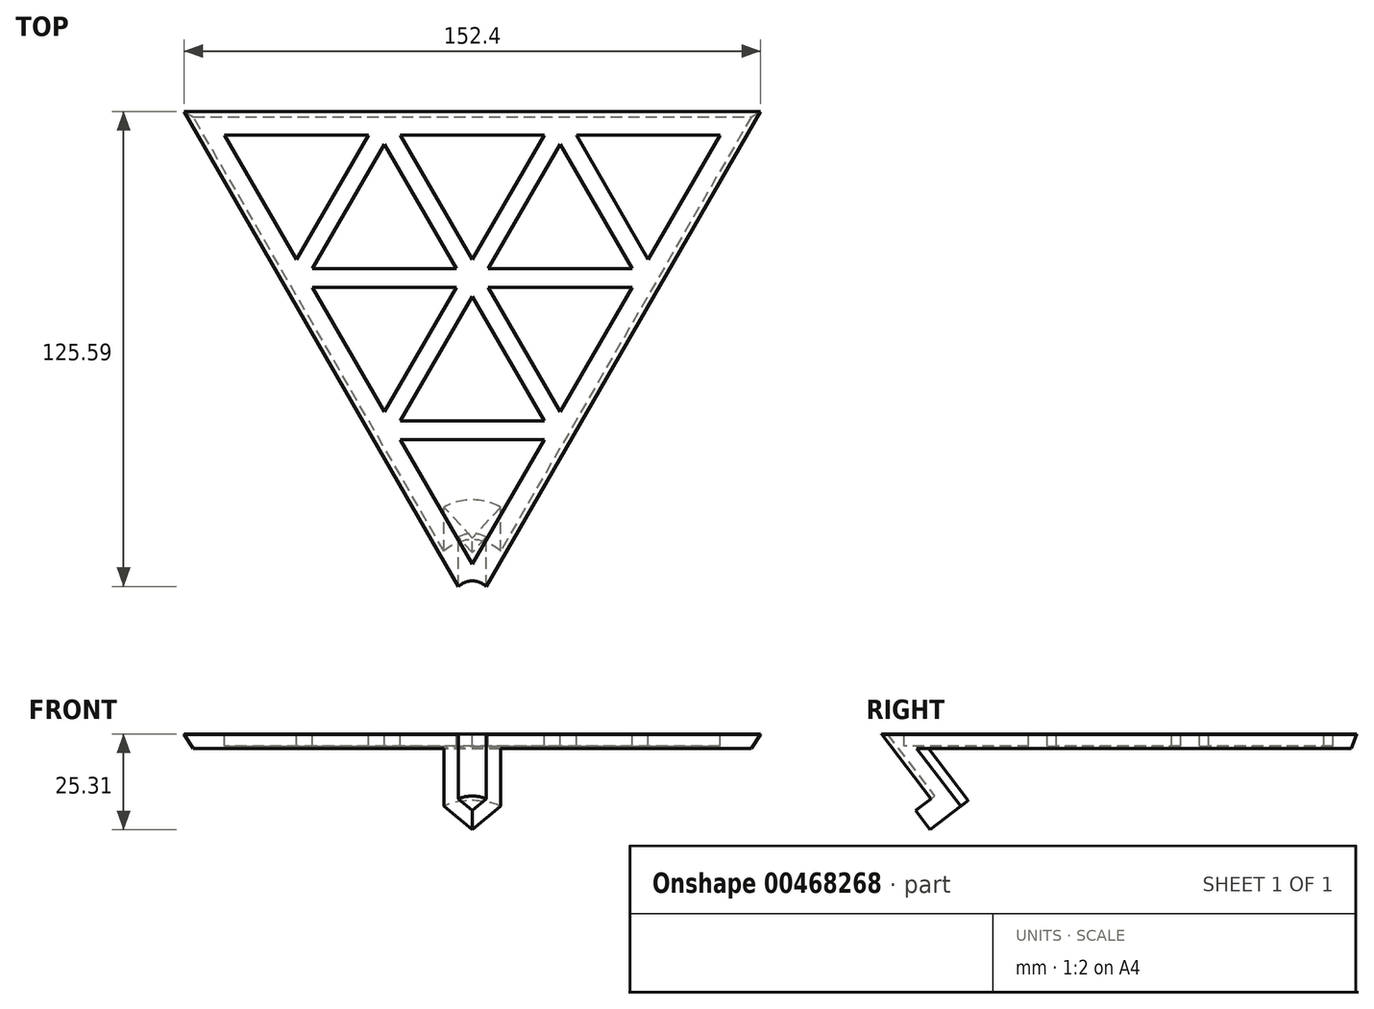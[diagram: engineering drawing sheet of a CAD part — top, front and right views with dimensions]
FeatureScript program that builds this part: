
annotation { "Feature Type Name" : "Feature", "Feature Type Description" : "" }
export const myFeature = defineFeature(function(context is Context, id is Id, definition is map)
    precondition{}
    {
        {
            var Q0;
            Q0=qCreatedBy(makeId("Top.planeOp"),FACE);
            var sketch = newSketch(context, id + "F0", { "sketchPlane" : qUnion([Q0])});
            skLineSegment(sketch, "E0", {"start": v(-76.2, 0) * mm, "end": v(76.2, 0) * mm});
            skLineSegment(sketch, "E1", {"start": v(76.2, 0) * mm, "end": v(0, -131.98) * mm});
            skLineSegment(sketch, "E2", {"start": v(0, -131.98) * mm, "end": v(-76.2, 0) * mm});
            skSolve(sketch);
        }
        {
            var Q0;
            Q0 = qSketchRegion(id + "F0", true);
            extrude(context, id + "F1", {"entities" : qUnion([Q0]), "depth" : 3.8 * mm});
        }
        {
            var Q0;
            Q0=makeQuery(id+"F1.opExtrude","CAP_EDGE",EDGE,{"disambiguationData":[OSD([sQuery(id+"F0.wireOp",EDGE,"E2")])],"isStart":true});
            var Q1;
            Q1=makeQuery(id+"F1.opExtrude","CAP_EDGE",EDGE,{"disambiguationData":[OSD([sQuery(id+"F0.wireOp",EDGE,"E1")])],"isStart":true});
            var Q2;
            Q2=makeQuery(id+"F1.opExtrude","CAP_EDGE",EDGE,{"disambiguationData":[OSD([sQuery(id+"F0.wireOp",EDGE,"E0")])],"isStart":true});
            chamfer(context, id + "F2", {"entities" : qUnion([Q0, Q1, Q2]), "chamferType" : ChamferType.OFFSET_ANGLE, "width" : 1.4 * mm, "oppositeDirection" : false, "angle" : 69.1 * degree, "tangentPropagation" : true});
        }
        {
            var Q0;
            Q0=makeQuery(id+"F1.opExtrude","CAP_FACE",FACE,{"disambiguationData":[OSD([sQuery(id+"F0.wireOp",EDGE,"E0"),sQuery(id+"F0.wireOp",EDGE,"E1"),sQuery(id+"F0.wireOp",EDGE,"E2")])],"isStart":false});
            var sketch = newSketch(context, id + "F3", { "sketchPlane" : qUnion([Q0])});
            skLineSegment(sketch, "E3", {"start": v(0, 0) * mm, "end": v(0, -131.98) * mm, "construction": true});
            skLineSegment(sketch, "E4", {"start": v(38.1, -66) * mm, "end": v(-76.2, 0) * mm, "construction": true});
            skLineSegment(sketch, "E5", {"start": v(-38.1, -66) * mm, "end": v(76.2, 0) * mm, "construction": true});
            skPoint(sketch, "E6", {"position": v(0, -44) * mm});
            skSolve(sketch);
        }
        {
            var Q0;
            Q0=qCreatedBy(makeId("Right.planeOp"),FACE);
            var sketch = newSketch(context, id + "F4", { "sketchPlane" : qUnion([Q0])});
            skPoint(sketch, "E7", {"position": v(-44, 3.81) * mm});
            skLineSegment(sketch, "E8", {"start": v(-44, 3.81) * mm, "end": v(-44, 53.17) * mm, "construction": true});
            skSolve(sketch);
        }
        {
            var Q0;
            Q0=makeQuery(id+"F1.opExtrude","CAP_FACE",FACE,{"disambiguationData":[OSD([sQuery(id+"F0.wireOp",EDGE,"E0"),sQuery(id+"F0.wireOp",EDGE,"E1"),sQuery(id+"F0.wireOp",EDGE,"E2")])],"isStart":false});
            var sketch = newSketch(context, id + "F5", { "sketchPlane" : qUnion([Q0])});
            skLineSegment(sketch, "E9", {"start": v(-46.49, -39.09) * mm, "end": v(-27.5, -6.19) * mm});
            skLineSegment(sketch, "E10", {"start": v(-27.5, -6.19) * mm, "end": v(-65.48, -6.19) * mm});
            skLineSegment(sketch, "E11", {"start": v(-42.24, -46.45) * mm, "end": v(-23.24, -79.35) * mm});
            skLineSegment(sketch, "E12", {"start": v(-23.24, -79.35) * mm, "end": v(-4.25, -46.45) * mm});
            skLineSegment(sketch, "E13", {"start": v(-4.25, -46.45) * mm, "end": v(-42.24, -46.45) * mm});
            skLineSegment(sketch, "E14", {"start": v(-42.24, -41.54) * mm, "end": v(-23.24, -8.64) * mm});
            skLineSegment(sketch, "E15", {"start": v(-23.24, -8.64) * mm, "end": v(-4.25, -41.54) * mm});
            skLineSegment(sketch, "E16", {"start": v(-4.25, -41.54) * mm, "end": v(-42.24, -41.54) * mm});
            skLineSegment(sketch, "E17", {"start": v(-19, -6.19) * mm, "end": v(0, -39.09) * mm});
            skLineSegment(sketch, "E18", {"start": v(0, -39.09) * mm, "end": v(19, -6.19) * mm});
            skLineSegment(sketch, "E19", {"start": v(19, -6.19) * mm, "end": v(-19, -6.19) * mm});
            skLineSegment(sketch, "E20", {"start": v(4.25, -41.54) * mm, "end": v(23.24, -8.64) * mm});
            skLineSegment(sketch, "E21", {"start": v(23.24, -8.64) * mm, "end": v(42.24, -41.54) * mm});
            skLineSegment(sketch, "E22", {"start": v(42.24, -41.54) * mm, "end": v(4.25, -41.54) * mm});
            skLineSegment(sketch, "E23", {"start": v(27.5, -6.19) * mm, "end": v(46.49, -39.09) * mm});
            skLineSegment(sketch, "E24", {"start": v(46.49, -39.09) * mm, "end": v(65.48, -6.19) * mm});
            skLineSegment(sketch, "E25", {"start": v(65.48, -6.19) * mm, "end": v(27.5, -6.19) * mm});
            skLineSegment(sketch, "E26", {"start": v(-19, -81.8) * mm, "end": v(0, -48.9) * mm});
            skLineSegment(sketch, "E27", {"start": v(0, -48.9) * mm, "end": v(19, -81.8) * mm});
            skLineSegment(sketch, "E28", {"start": v(19, -81.8) * mm, "end": v(-19, -81.8) * mm});
            skLineSegment(sketch, "E29", {"start": v(42.24, -46.45) * mm, "end": v(23.24, -79.35) * mm});
            skLineSegment(sketch, "E30", {"start": v(23.24, -79.35) * mm, "end": v(4.25, -46.45) * mm});
            skLineSegment(sketch, "E31", {"start": v(4.25, -46.45) * mm, "end": v(42.24, -46.45) * mm});
            skLineSegment(sketch, "E32", {"start": v(-19, -86.7) * mm, "end": v(0, -119.6) * mm});
            skLineSegment(sketch, "E33", {"start": v(0, -119.6) * mm, "end": v(19, -86.7) * mm});
            skLineSegment(sketch, "E34", {"start": v(19, -86.7) * mm, "end": v(-19, -86.7) * mm});
            skLineSegment(sketch, "E35", {"start": v(-65.48, -6.19) * mm, "end": v(-46.49, -39.09) * mm});
            skLineSegment(sketch, "E36", {"start": v(-38.1, -66) * mm, "end": v(76.2, 0) * mm, "construction": true});
            skLineSegment(sketch, "E37", {"start": v(-76.2, 0) * mm, "end": v(38.1, -66) * mm, "construction": true});
            skCircle(sketch, "E38", {"center": v(0, -44) * mm, "radius": 4.9 * mm, "construction": true});
            skSolve(sketch);
        }
        {
            var Q0;
            Q0=qCreatedBy(makeId("Right.planeOp"),FACE);
            var sketch = newSketch(context, id + "F6", { "sketchPlane" : qUnion([Q0])});
            skLineSegment(sketch, "E39", {"start": v(-133.02, 5.01) * mm, "end": v(-125.3, -5.08) * mm});
            skLineSegment(sketch, "E40", {"start": v(-133.02, 5.01) * mm, "end": v(-127.97, 8.87) * mm});
            skLineSegment(sketch, "E41", {"start": v(-127.97, 8.87) * mm, "end": v(-120.26, -1.23) * mm});
            skLineSegment(sketch, "E42", {"start": v(-120.26, -1.23) * mm, "end": v(-125.3, -5.08) * mm});
            skSolve(sketch);
        }
        {
            var Q0;
            Q0=makeQuery(id+"F6.imprint","IMPRINT",FACE,{"disambiguationData":[TD([[makeQuery(id+"F6.imprint","IMPRINT",EDGE,{"derivedFrom":sQuery(id+"F6.wireOp",EDGE,"E39")}),1.0]])]});
            var Q1;
            Q1=sQuery(id+"F6.wireOp",EDGE,"E39");
            revolve(context, id + "F7", {"operationType" : NewBodyOperationType.REMOVE, "entities" : qUnion([Q0]), "axis" : qUnion([Q1]), "revolveType" : RevolveType.FULL, "oppositeDirection" : true});
        }
        {
            var Q0;
            Q0=makeQuery(id+"F6.imprint","IMPRINT",FACE,{"disambiguationData":[TD([[makeQuery(id+"F6.imprint","IMPRINT",EDGE,{"derivedFrom":sQuery(id+"F6.wireOp",EDGE,"E39")}),1.0]])]});
            var sketch = newSketch(context, id + "F8", { "sketchPlane" : qUnion([Q0])});
            skLineSegment(sketch, "E43", {"start": v(-123.14, 2.54) * mm, "end": v(-111.57, -12.6) * mm});
            skLineSegment(sketch, "E44", {"start": v(-111.57, -12.6) * mm, "end": v(-116.62, -16.45) * mm});
            skLineSegment(sketch, "E45", {"start": v(-116.62, -16.45) * mm, "end": v(-112.76, -21.5) * mm});
            skLineSegment(sketch, "E46", {"start": v(-112.76, -21.5) * mm, "end": v(-102.67, -13.79) * mm});
            skLineSegment(sketch, "E47", {"start": v(-102.67, -13.79) * mm, "end": v(-115.15, 2.54) * mm});
            skLineSegment(sketch, "E48", {"start": v(-123.14, 2.54) * mm, "end": v(-115.15, 2.54) * mm});
            skSolve(sketch);
        }
        {
            var Q0;
            {var subQ0=sQuery(id+"F8.wireOp",EDGE,"E44");Q0=makeQuery(id+"F8.imprint","IMPRINT",FACE,{"disambiguationData":[TD([[makeQuery(id+"F8.imprint","IMPRINT",EDGE,{"derivedFrom":subQ0}),1.0]])]});}
            var Q1;
            Q1=sQuery(id+"F8.wireOp",EDGE,"E45");
            revolve(context, id + "F9", {"operationType" : NewBodyOperationType.ADD, "entities" : qUnion([Q0]), "axis" : qUnion([Q1]), "revolveType" : RevolveType.FULL});
        }
        {
            var Q0;
            Q0=makeQuery(id+"F9.opRevolve","SWEPT_FACE",FACE,{"disambiguationData":[OSD([sQuery(id+"F8.wireOp",EDGE,"E46")])]});
            var sketch = newSketch(context, id + "F10", { "sketchPlane" : qUnion([Q0])});
            skLineSegment(sketch, "E49", {"start": v(7.46, 92.39) * mm, "end": v(0, 102.66) * mm});
            skLineSegment(sketch, "E50", {"start": v(0, 102.66) * mm, "end": v(-7.46, 92.39) * mm});
            skArc(sketch, "E51", {"start": v(7.46, 92.39) * mm, "mid": v(0, 115.36) * mm, "end": v(-7.46, 92.39) * mm});
            skSolve(sketch);
        }
        {
            var Q0;
            Q0 = qSketchRegion(id + "F10", true);
            extrude(context, id + "F11", {"entities" : qUnion([Q0]), "operationType" : NewBodyOperationType.REMOVE, "oppositeDirection" : true, "depth" : 25.4 * mm});
        }
        {
            var Q0;
            Q0 = qSketchRegion(id + "F5", true);
            extrude(context, id + "F12", {"entities" : qUnion([Q0]), "operationType" : NewBodyOperationType.REMOVE, "oppositeDirection" : true, "depth" : 3.17 * mm});
        }
    });
